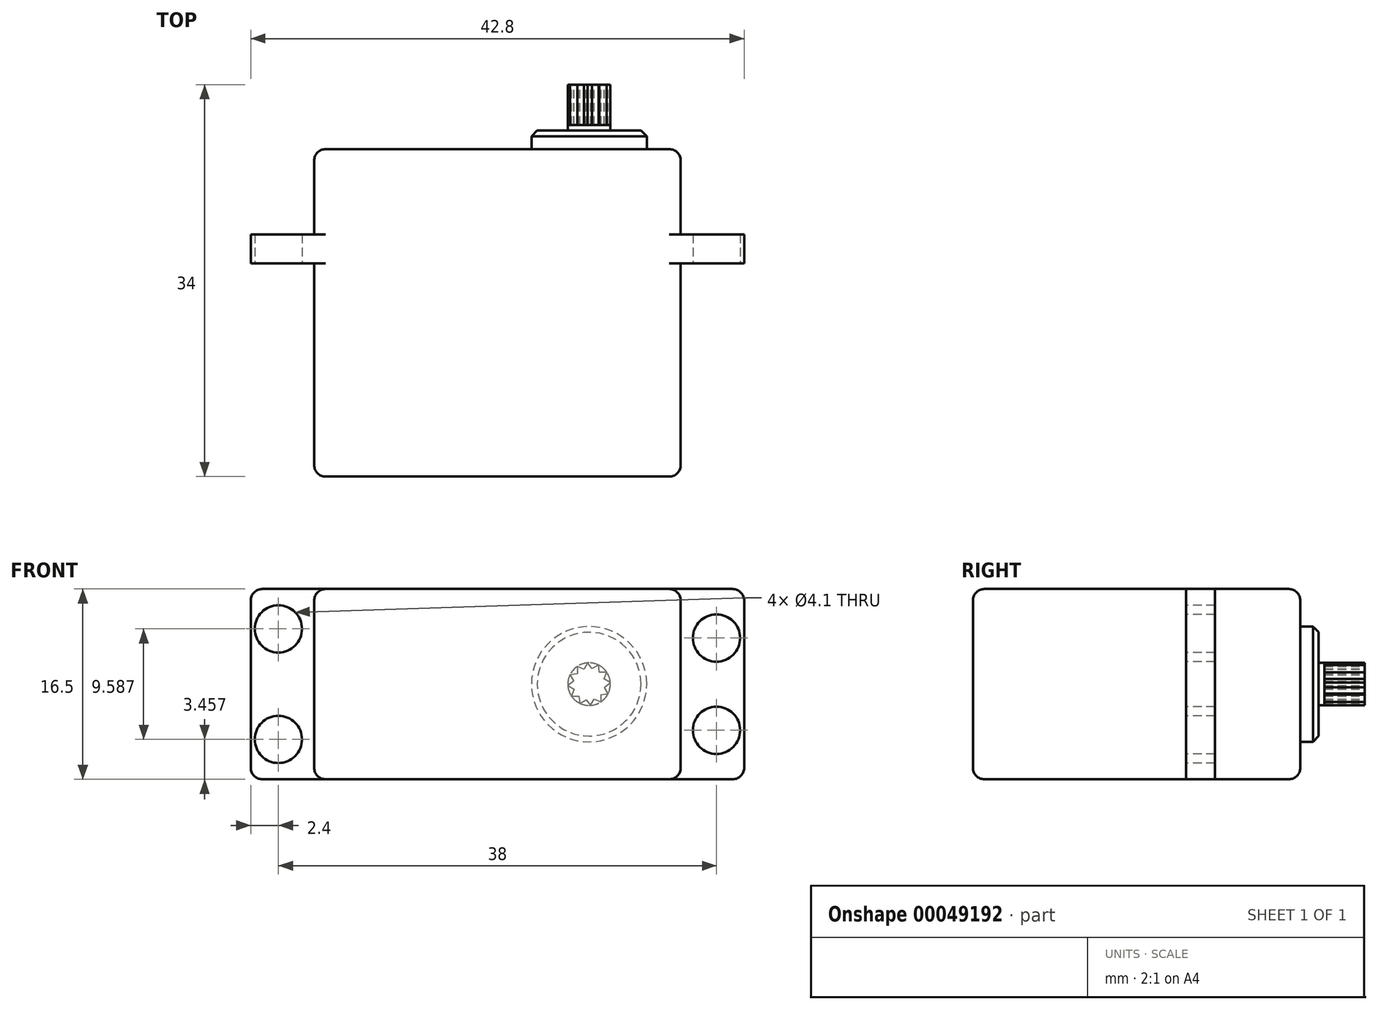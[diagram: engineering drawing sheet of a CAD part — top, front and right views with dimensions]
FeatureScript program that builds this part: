
annotation { "Feature Type Name" : "Feature", "Feature Type Description" : "" }
export const myFeature = defineFeature(function(context is Context, id is Id, definition is map)
    precondition{}
    {
        {
            var Q0;
            Q0=qCreatedBy(makeId("Top.planeOp"),FACE);
            var sketch = newSketch(context, id + "F0", { "sketchPlane" : qUnion([Q0])});
            skLineSegment(sketch, "E0.bottom", {"start": v(-15.9, 14.2) * mm, "end": v(15.9, 14.2) * mm});
            skLineSegment(sketch, "E0.top", {"start": v(-15.9, -14.2) * mm, "end": v(15.9, -14.2) * mm});
            skLineSegment(sketch, "E0.left", {"start": v(-15.9, 14.2) * mm, "end": v(-15.9, -14.2) * mm});
            skLineSegment(sketch, "E0.right", {"start": v(15.9, 14.2) * mm, "end": v(15.9, -14.2) * mm});
            skPoint(sketch, "E1", {"position": v(15.9, 0) * mm});
            skLineSegment(sketch, "E2", {"start": v(15.9, 0) * mm, "end": v(-15.9, 0) * mm, "construction": true});
            skPoint(sketch, "E3", {"position": v(0, 0) * mm});
            skLineSegment(sketch, "E4", {"start": v(-15.9, 6.8) * mm, "end": v(15.9, 6.8) * mm});
            skLineSegment(sketch, "E5", {"start": v(-15.9, 4.3) * mm, "end": v(15.9, 4.3) * mm});
            skLineSegment(sketch, "E6.left", {"start": v(-15.9, 6.8) * mm, "end": v(-15.9, 6.8) * mm});
            skLineSegment(sketch, "E7", {"start": v(-19, 4.3) * mm, "end": v(-19, 6.8) * mm, "construction": true});
            skLineSegment(sketch, "E8", {"start": v(19, 6.8) * mm, "end": v(19, 4.3) * mm, "construction": true});
            skLineSegment(sketch, "E9", {"start": v(-19, 6.8) * mm, "end": v(-21.4, 6.8) * mm});
            skLineSegment(sketch, "E10", {"start": v(-21.4, 6.8) * mm, "end": v(-21.4, 4.3) * mm});
            skLineSegment(sketch, "E11", {"start": v(-21.4, 4.3) * mm, "end": v(-19, 4.3) * mm});
            skLineSegment(sketch, "E12", {"start": v(19, 6.8) * mm, "end": v(21.4, 6.8) * mm});
            skLineSegment(sketch, "E13", {"start": v(21.4, 6.8) * mm, "end": v(21.4, 4.3) * mm});
            skLineSegment(sketch, "E14", {"start": v(21.4, 4.3) * mm, "end": v(19, 4.3) * mm});
            skLineSegment(sketch, "E15", {"start": v(-19, 6.8) * mm, "end": v(-15.9, 6.8) * mm});
            skLineSegment(sketch, "E16", {"start": v(-19, 4.3) * mm, "end": v(-15.9, 4.3) * mm});
            skLineSegment(sketch, "E17", {"start": v(15.9, 4.3) * mm, "end": v(19, 4.3) * mm});
            skLineSegment(sketch, "E18", {"start": v(15.9, 6.8) * mm, "end": v(19, 6.8) * mm});
            skSolve(sketch);
        }
        {
            var Q0;
            {var subQ2=sQuery(id+"F0.wireOp",EDGE,"E0.bottom");Q0=makeQuery(id+"F0.imprint","IMPRINT",FACE,{"disambiguationData":[TD([[makeQuery(id+"F0.imprint","IMPRINT",EDGE,{"derivedFrom":subQ2}),-1.0]])]});}
            var Q1;
            {var subQ1=sQuery(id+"F0.wireOp",EDGE,"E4");Q1=makeQuery(id+"F0.imprint","IMPRINT",FACE,{"disambiguationData":[TD([[makeQuery(id+"F0.imprint","IMPRINT",EDGE,{"derivedFrom":subQ1}),-1.0]])]});}
            var Q2;
            {var subQ2=sQuery(id+"F0.wireOp",EDGE,"E0.top");Q2=makeQuery(id+"F0.imprint","IMPRINT",FACE,{"disambiguationData":[TD([[makeQuery(id+"F0.imprint","IMPRINT",EDGE,{"derivedFrom":subQ2}),1.0]])]});}
            var Q3;
            {var subQ1=sQuery(id+"F0.wireOp",EDGE,"09e22627-e60c-491d-84b8-1f82f3b54810");Q3=makeQuery(id+"F0.imprint","IMPRINT",FACE,{"disambiguationData":[TD([[makeQuery(id+"F0.imprint","IMPRINT",EDGE,{"derivedFrom":subQ1}),1.0]])]});}
            var Q4;
            {var subQ1=sQuery(id+"F0.wireOp",EDGE,"9076f290-2de4-49c5-82f5-c9286705dbb7");Q4=makeQuery(id+"F0.imprint","IMPRINT",FACE,{"disambiguationData":[TD([[makeQuery(id+"F0.imprint","IMPRINT",EDGE,{"derivedFrom":subQ1}),-1.0]])]});}
            var Q5;
            Q5=makeQuery(id+"F0.imprint","IMPRINT",FACE,{"disambiguationData":[TD([[makeQuery(id+"F0.imprint","IMPRINT",EDGE,{"derivedFrom":sQuery(id+"F0.wireOp",EDGE,"E9")}),1.0]])]});
            var Q6;
            Q6=makeQuery(id+"F0.imprint","IMPRINT",FACE,{"disambiguationData":[TD([[makeQuery(id+"F0.imprint","IMPRINT",EDGE,{"derivedFrom":sQuery(id+"F0.wireOp",EDGE,"E12")}),-1.0]])]});
            extrude(context, id + "F1", {"entities" : qUnion([Q0, Q1, Q2, Q3, Q4, Q5, Q6]), "depth" : 16.5 * mm});
        }
        {
            var Q0;
            Q0=makeQuery(id+"F1.opExtrude","SWEPT_FACE",FACE,{"disambiguationData":[OSD([sQuery(id+"F0.wireOp",EDGE,"c4af46d5-3eda-48fc-baeb-3fe5783b968a"),sQuery(id+"F0.wireOp",EDGE,"E11")])]});
            var sketch = newSketch(context, id + "F2", { "sketchPlane" : qUnion([Q0])});
            skLineSegment(sketch, "E19.0", {"start": v(-21.4, 16.5) * mm, "end": v(-15.9, 16.5) * mm});
            skLineSegment(sketch, "E20.0", {"start": v(-19, 0) * mm, "end": v(-15.9, 0) * mm});
            skLineSegment(sketch, "E21", {"start": v(-19, 0) * mm, "end": v(-19, 16.5) * mm, "construction": true});
            skLineSegment(sketch, "E22.0", {"start": v(19, 0) * mm, "end": v(21.4, 0) * mm});
            skLineSegment(sketch, "E23.0", {"start": v(15.9, 16.5) * mm, "end": v(21.4, 16.5) * mm});
            skLineSegment(sketch, "E24", {"start": v(19, 0) * mm, "end": v(19, 16.5) * mm, "construction": true});
            skSolve(sketch);
        }
        {
            var Q0;
            {var subQ1=sQuery(id+"F0.wireOp",EDGE,"E11");Q0=makeQuery(id+"F2.imprint","IMPRINT",FACE,{"disambiguationData":[TD([[makeQuery(id+"F2.imprint","IMPRINT",EDGE,{"derivedFrom":makeQuery(id+"F1.opExtrude","SWEPT_EDGE",EDGE,{"disambiguationData":[OSD([sQuery(id+"F0.wireOp",EDGE,"E10"),subQ1])]})}),1.0]])]});}
            cPlane(context, id + "F3", {"entities" : qUnion([Q0]), "cplaneType" : CPlaneType.OFFSET, "offset" : 0 * mm, "width" : 150 * mm, "height" : 150 * mm});
        }
        {
            var Q0;
            Q0=qCreatedBy(id+"F3.planeOp",FACE);
            var sketch = newSketch(context, id + "F4", { "sketchPlane" : qUnion([Q0])});
            skLineSegment(sketch, "E25.0", {"start": v(-19, 0) * mm, "end": v(-15.9, 0) * mm});
            skPoint(sketch, "E26", {"position": v(-19, 8.25) * mm});
            skPoint(sketch, "E27", {"position": v(19, 8.25) * mm});
            skPoint(sketch, "E28.orphan", {"position": v(19, 16.5) * mm});
            skPoint(sketch, "E29.1.start.orphan", {"position": v(19, 0) * mm});
            skPoint(sketch, "E30.orphan", {"position": v(-19, 16.5) * mm});
            skPoint(sketch, "E31.0.start.orphan", {"position": v(-19, 0) * mm});
            skLineSegment(sketch, "E32", {"start": v(-19, 8.25) * mm, "end": v(-19, 13.04) * mm, "construction": true});
            skLineSegment(sketch, "E33", {"start": v(-19, 8.25) * mm, "end": v(-19, 3.46) * mm, "construction": true});
            skLineSegment(sketch, "E34", {"start": v(19, 8.25) * mm, "end": v(19, 12.25) * mm, "construction": true});
            skLineSegment(sketch, "E35", {"start": v(19, 8.25) * mm, "end": v(19, 4.25) * mm, "construction": true});
            skCircle(sketch, "E36", {"center": v(-19, 13.04) * mm, "radius": 2.05 * mm});
            skCircle(sketch, "E37", {"center": v(-19, 3.46) * mm, "radius": 2.05 * mm});
            skCircle(sketch, "E38", {"center": v(19, 12.25) * mm, "radius": 2.05 * mm});
            skCircle(sketch, "E39", {"center": v(19, 4.25) * mm, "radius": 2.05 * mm});
            skSolve(sketch);
        }
        {
            var Q0;
            Q0=qSketchRegion(id+"F4",true);
            extrude(context, id + "F5", {"entities" : qUnion([Q0]), "operationType" : NewBodyOperationType.REMOVE, "endBound" : BoundingType.THROUGH_ALL, "oppositeDirection" : true, "depth" : 25 * mm});
        }
        {
            var Q0;
            Q0=makeQuery(id+"F1.opExtrude","SWEPT_FACE",FACE,{"disambiguationData":[OSD([sQuery(id+"F0.wireOp",EDGE,"E0.bottom")])]});
            var sketch = newSketch(context, id + "F6", { "sketchPlane" : qUnion([Q0])});
            skLineSegment(sketch, "E40", {"start": v(-15.9, 8.25) * mm, "end": v(0, 8.25) * mm, "construction": true});
            skPoint(sketch, "E41.orphan", {"position": v(15.9, 8.25) * mm});
            skPoint(sketch, "E42", {"position": v(-7.95, 8.25) * mm});
            skCircle(sketch, "E43", {"center": v(-7.95, 8.25) * mm, "radius": 5 * mm});
            skLineSegment(sketch, "E44.6", {"start": v(11.12, 7.62) * mm, "end": v(11.12, 7.62) * mm});
            skLineSegment(sketch, "E44.7", {"start": v(11.12, 7.62) * mm, "end": v(11.12, 7.62) * mm});
            skLineSegment(sketch, "E44.8", {"start": v(11.12, 7.62) * mm, "end": v(11.12, 7.62) * mm});
            skLineSegment(sketch, "E44.9", {"start": v(11.12, 7.62) * mm, "end": v(11.12, 7.62) * mm});
            skLineSegment(sketch, "E44.10", {"start": v(11.12, 7.62) * mm, "end": v(11.12, 7.62) * mm});
            skLineSegment(sketch, "E44.11", {"start": v(11.12, 7.62) * mm, "end": v(11.12, 7.62) * mm});
            skLineSegment(sketch, "E44.12", {"start": v(11.12, 7.62) * mm, "end": v(11.12, 7.62) * mm});
            skLineSegment(sketch, "E44.13", {"start": v(11.12, 7.62) * mm, "end": v(11.12, 7.62) * mm});
            skLineSegment(sketch, "E44.14", {"start": v(11.12, 7.62) * mm, "end": v(11.12, 7.62) * mm});
            skLineSegment(sketch, "E44.15", {"start": v(11.12, 7.62) * mm, "end": v(11.12, 7.62) * mm});
            skLineSegment(sketch, "E44.16", {"start": v(11.12, 7.62) * mm, "end": v(11.12, 7.62) * mm});
            skLineSegment(sketch, "E44.17", {"start": v(11.12, 7.62) * mm, "end": v(11.12, 7.62) * mm});
            skLineSegment(sketch, "E44.18", {"start": v(11.12, 7.62) * mm, "end": v(11.12, 7.62) * mm});
            skLineSegment(sketch, "E44.19", {"start": v(11.12, 7.62) * mm, "end": v(11.12, 7.62) * mm});
            skCircle(sketch, "E45", {"center": v(-7.95, 8.25) * mm, "radius": 1.85 * mm});
            skSolve(sketch);
        }
        {
            var Q0;
            Q0=makeQuery(id+"F6.imprint","IMPRINT",FACE,{"disambiguationData":[TD([[makeQuery(id+"F6.imprint","IMPRINT",EDGE,{"derivedFrom":sQuery(id+"F6.wireOp",EDGE,"E43")}),1.0]])]});
            var Q1;
            Q1=makeQuery(id+"F6.imprint","IMPRINT",FACE,{"disambiguationData":[TD([[makeQuery(id+"F6.imprint","IMPRINT",EDGE,{"derivedFrom":sQuery(id+"F6.wireOp",EDGE,"E45")}),1.0]])]});
            var Q2;
            Q2=sQuery(id+"F6.wireOp",EDGE,"E43");
            extrude(context, id + "F7", {"entities" : qUnion([Q0, Q1]), "operationType" : NewBodyOperationType.ADD, "surfaceEntities" : qUnion([Q2]), "depth" : 1.6 * mm});
        }
        {
            var Q0;
            Q0=makeQuery(id+"F7.opExtrude","CAP_EDGE",EDGE,{"disambiguationData":[OSD([sQuery(id+"F6.wireOp",EDGE,"E43")])],"isStart":false});
            chamfer(context, id + "F8", {"entities" : qUnion([Q0]), "width" : 0.5 * mm, "tangentPropagation" : true});
        }
        {
            var Q0;
            Q0=makeQuery(id+"F7.opExtrude","CAP_FACE",FACE,{"disambiguationData":[OSD([sQuery(id+"F6.wireOp",EDGE,"E43")])],"isStart":false});
            var sketch = newSketch(context, id + "F9", { "sketchPlane" : qUnion([Q0])});
            skCircle(sketch, "E46.0", {"center": v(-7.95, 8.25) * mm, "radius": 1.85 * mm});
            skSolve(sketch);
        }
        {
            var Q0;
            Q0=makeQuery(id+"F9.imprint","IMPRINT",FACE,{"disambiguationData":[TD([[makeQuery(id+"F9.imprint","IMPRINT",EDGE,{"derivedFrom":sQuery(id+"F9.wireOp",EDGE,"E46.0")}),1.0]])]});
            extrude(context, id + "F10", {"entities" : qUnion([Q0]), "depth" : 4 * mm});
        }
        {
            var Q0;
            Q0=makeQuery(id+"F10.opExtrude","CAP_FACE",FACE,{"disambiguationData":[OSD([sQuery(id+"F9.wireOp",EDGE,"E46.0")])],"isStart":false});
            var sketch = newSketch(context, id + "F11", { "sketchPlane" : qUnion([Q0])});
            skCircle(sketch, "E47", {"center": v(-7.95, 8.25) * mm, "radius": 1.37 * mm});
            skLineSegment(sketch, "E48", {"start": v(-7.82, 10.1) * mm, "end": v(-7.5, 9.54) * mm});
            skLineSegment(sketch, "E49", {"start": v(-7.5, 9.54) * mm, "end": v(-6.92, 9.78) * mm});
            skLineSegment(sketch, "E50", {"start": v(-6.92, 9.78) * mm, "end": v(-6.92, 9.15) * mm});
            skLineSegment(sketch, "E51", {"start": v(-6.92, 9.15) * mm, "end": v(-6.3, 9.06) * mm});
            skLineSegment(sketch, "E52", {"start": v(-6.3, 9.06) * mm, "end": v(-6.6, 8.51) * mm});
            skLineSegment(sketch, "E53", {"start": v(-6.6, 8.51) * mm, "end": v(-6.1, 8.12) * mm});
            skLineSegment(sketch, "E54", {"start": v(-6.1, 8.12) * mm, "end": v(-6.66, 7.8) * mm});
            skLineSegment(sketch, "E55", {"start": v(-6.66, 7.8) * mm, "end": v(-6.42, 7.22) * mm});
            skLineSegment(sketch, "E56", {"start": v(-6.42, 7.22) * mm, "end": v(-7.05, 7.22) * mm});
            skLineSegment(sketch, "E57", {"start": v(-7.05, 7.22) * mm, "end": v(-7.14, 6.6) * mm});
            skLineSegment(sketch, "E58", {"start": v(-7.14, 6.6) * mm, "end": v(-7.69, 6.9) * mm});
            skLineSegment(sketch, "E59", {"start": v(-7.69, 6.9) * mm, "end": v(-8.08, 6.4) * mm});
            skLineSegment(sketch, "E60", {"start": v(-8.08, 6.4) * mm, "end": v(-8.4, 6.96) * mm});
            skLineSegment(sketch, "E61", {"start": v(-8.4, 6.96) * mm, "end": v(-8.98, 6.72) * mm});
            skLineSegment(sketch, "E62", {"start": v(-8.98, 6.72) * mm, "end": v(-8.98, 7.35) * mm});
            skLineSegment(sketch, "E63", {"start": v(-8.98, 7.35) * mm, "end": v(-9.6, 7.44) * mm});
            skLineSegment(sketch, "E64", {"start": v(-9.6, 7.44) * mm, "end": v(-9.3, 7.99) * mm});
            skLineSegment(sketch, "E65", {"start": v(-9.3, 7.99) * mm, "end": v(-9.8, 8.38) * mm});
            skLineSegment(sketch, "E66", {"start": v(-9.48, 9.28) * mm, "end": v(-8.85, 9.28) * mm});
            skLineSegment(sketch, "E67", {"start": v(-8.85, 9.28) * mm, "end": v(-8.76, 9.9) * mm});
            skLineSegment(sketch, "E68", {"start": v(-8.76, 9.9) * mm, "end": v(-8.21, 9.6) * mm});
            skLineSegment(sketch, "E69", {"start": v(-8.21, 9.6) * mm, "end": v(-7.82, 10.1) * mm});
            skLineSegment(sketch, "E70", {"start": v(-9.8, 8.38) * mm, "end": v(-9.24, 8.7) * mm});
            skLineSegment(sketch, "E71", {"start": v(-9.24, 8.7) * mm, "end": v(-9.48, 9.28) * mm});
            skSolve(sketch);
        }
        {
            var Q0;
            {var subQ2=sQuery(id+"F11.wireOp",EDGE,"E66");Q0=makeQuery(id+"F11.imprint","IMPRINT",FACE,{"disambiguationData":[TD([[makeQuery(id+"F11.imprint","IMPRINT",EDGE,{"derivedFrom":subQ2}),1.0]])]});}
            var Q1;
            {var subQ2=sQuery(id+"F11.wireOp",EDGE,"E70");Q1=makeQuery(id+"F11.imprint","IMPRINT",FACE,{"disambiguationData":[TD([[makeQuery(id+"F11.imprint","IMPRINT",EDGE,{"derivedFrom":subQ2}),1.0]])]});}
            var Q2;
            {var subQ2=sQuery(id+"F11.wireOp",EDGE,"E64");Q2=makeQuery(id+"F11.imprint","IMPRINT",FACE,{"disambiguationData":[TD([[makeQuery(id+"F11.imprint","IMPRINT",EDGE,{"derivedFrom":subQ2}),1.0]])]});}
            var Q3;
            {var subQ2=sQuery(id+"F11.wireOp",EDGE,"E62");Q3=makeQuery(id+"F11.imprint","IMPRINT",FACE,{"disambiguationData":[TD([[makeQuery(id+"F11.imprint","IMPRINT",EDGE,{"derivedFrom":subQ2}),1.0]])]});}
            var Q4;
            {var subQ2=sQuery(id+"F11.wireOp",EDGE,"E60");Q4=makeQuery(id+"F11.imprint","IMPRINT",FACE,{"disambiguationData":[TD([[makeQuery(id+"F11.imprint","IMPRINT",EDGE,{"derivedFrom":subQ2}),1.0]])]});}
            var Q5;
            {var subQ2=sQuery(id+"F11.wireOp",EDGE,"E58");Q5=makeQuery(id+"F11.imprint","IMPRINT",FACE,{"disambiguationData":[TD([[makeQuery(id+"F11.imprint","IMPRINT",EDGE,{"derivedFrom":subQ2}),1.0]])]});}
            var Q6;
            {var subQ2=sQuery(id+"F11.wireOp",EDGE,"E56");Q6=makeQuery(id+"F11.imprint","IMPRINT",FACE,{"disambiguationData":[TD([[makeQuery(id+"F11.imprint","IMPRINT",EDGE,{"derivedFrom":subQ2}),1.0]])]});}
            var Q7;
            {var subQ2=sQuery(id+"F11.wireOp",EDGE,"E54");Q7=makeQuery(id+"F11.imprint","IMPRINT",FACE,{"disambiguationData":[TD([[makeQuery(id+"F11.imprint","IMPRINT",EDGE,{"derivedFrom":subQ2}),1.0]])]});}
            var Q8;
            {var subQ2=sQuery(id+"F11.wireOp",EDGE,"E52");Q8=makeQuery(id+"F11.imprint","IMPRINT",FACE,{"disambiguationData":[TD([[makeQuery(id+"F11.imprint","IMPRINT",EDGE,{"derivedFrom":subQ2}),1.0]])]});}
            var Q9;
            {var subQ2=sQuery(id+"F11.wireOp",EDGE,"E50");Q9=makeQuery(id+"F11.imprint","IMPRINT",FACE,{"disambiguationData":[TD([[makeQuery(id+"F11.imprint","IMPRINT",EDGE,{"derivedFrom":subQ2}),1.0]])]});}
            var Q10;
            {var subQ2=sQuery(id+"F11.wireOp",EDGE,"E48");Q10=makeQuery(id+"F11.imprint","IMPRINT",FACE,{"disambiguationData":[TD([[makeQuery(id+"F11.imprint","IMPRINT",EDGE,{"derivedFrom":subQ2}),1.0]])]});}
            var Q11;
            {var subQ1=sQuery(id+"F11.wireOp",EDGE,"E68");Q11=makeQuery(id+"F11.imprint","IMPRINT",FACE,{"disambiguationData":[TD([[makeQuery(id+"F11.imprint","IMPRINT",EDGE,{"derivedFrom":subQ1}),1.0]])]});}
            extrude(context, id + "F12", {"entities" : qUnion([Q0, Q1, Q2, Q3, Q4, Q5, Q6, Q7, Q8, Q9, Q10, Q11]), "operationType" : NewBodyOperationType.REMOVE, "oppositeDirection" : true, "depth" : 3.5 * mm});
        }
        {
            var Q0;
            Q0=makeQuery(id+"F1.opExtrude","SWEPT_FACE",FACE,{"disambiguationData":[OSD([sQuery(id+"F0.wireOp",EDGE,"E0.top")])]});
            var Q1;
            Q1=makeQuery(id+"F1.opExtrude","CAP_EDGE",EDGE,{"disambiguationData":[OSD([sQuery(id+"F0.wireOp",EDGE,"E0.bottom")])],"isStart":false});
            var Q2;
            {var subQ0=sQuery(id+"F0.wireOp",EDGE,"E0.right");Q2=makeQuery(id+"F1.opExtrude","CAP_EDGE",EDGE,{"disambiguationData":[OSD([subQ0]),TDD([makeQuery(id+"F0.imprint","IMPRINT",EDGE,{"disambiguationData":[TD([[makeQuery(id+"F0.imprint","INTERSECT",VERTEX,{"derivedFrom":[sQuery(id+"F0.wireOp",EDGE,"E0.top"),subQ0]}),1.0]])],"derivedFrom":subQ0})])],"isStart":false});}
            var Q3;
            {var subQ0=sQuery(id+"F0.wireOp",EDGE,"E0.right");Q3=makeQuery(id+"F1.opExtrude","CAP_EDGE",EDGE,{"disambiguationData":[OSD([subQ0]),TDD([makeQuery(id+"F0.imprint","IMPRINT",EDGE,{"disambiguationData":[TD([[makeQuery(id+"F0.imprint","INTERSECT",VERTEX,{"derivedFrom":[sQuery(id+"F0.wireOp",EDGE,"E0.top"),subQ0]}),1.0]])],"derivedFrom":subQ0})])],"isStart":true});}
            var Q4;
            {var subQ0=sQuery(id+"F0.wireOp",EDGE,"E0.left");Q4=makeQuery(id+"F1.opExtrude","CAP_EDGE",EDGE,{"disambiguationData":[OSD([subQ0]),TDD([makeQuery(id+"F0.imprint","IMPRINT",EDGE,{"disambiguationData":[TD([[makeQuery(id+"F0.imprint","INTERSECT",VERTEX,{"derivedFrom":[sQuery(id+"F0.wireOp",EDGE,"E0.top"),subQ0]}),1.0]])],"derivedFrom":subQ0})])],"isStart":true});}
            var Q5;
            {var subQ0=sQuery(id+"F0.wireOp",EDGE,"E0.left");Q5=makeQuery(id+"F1.opExtrude","CAP_EDGE",EDGE,{"disambiguationData":[OSD([subQ0]),TDD([makeQuery(id+"F0.imprint","IMPRINT",EDGE,{"disambiguationData":[TD([[makeQuery(id+"F0.imprint","INTERSECT",VERTEX,{"derivedFrom":[sQuery(id+"F0.wireOp",EDGE,"E0.top"),subQ0]}),1.0]])],"derivedFrom":subQ0})])],"isStart":false});}
            var Q6;
            Q6=makeQuery(id+"F1.opExtrude","SWEPT_EDGE",EDGE,{"disambiguationData":[OSD([sQuery(id+"F0.wireOp",EDGE,"E0.bottom"),sQuery(id+"F0.wireOp",EDGE,"E0.left")])]});
            var Q7;
            Q7=makeQuery(id+"F1.opExtrude","CAP_EDGE",EDGE,{"disambiguationData":[OSD([sQuery(id+"F0.wireOp",EDGE,"E0.bottom")])],"isStart":true});
            var Q8;
            {var subQ0=sQuery(id+"F0.wireOp",EDGE,"E0.right");Q8=makeQuery(id+"F1.opExtrude","CAP_EDGE",EDGE,{"disambiguationData":[OSD([subQ0]),TDD([makeQuery(id+"F0.imprint","IMPRINT",EDGE,{"disambiguationData":[TD([[makeQuery(id+"F0.imprint","INTERSECT",VERTEX,{"derivedFrom":[sQuery(id+"F0.wireOp",EDGE,"E0.bottom"),subQ0]}),-1.0]])],"derivedFrom":subQ0})])],"isStart":true});}
            var Q9;
            {var subQ0=sQuery(id+"F0.wireOp",EDGE,"E0.right");Q9=makeQuery(id+"F1.opExtrude","CAP_EDGE",EDGE,{"disambiguationData":[OSD([subQ0]),TDD([makeQuery(id+"F0.imprint","IMPRINT",EDGE,{"disambiguationData":[TD([[makeQuery(id+"F0.imprint","INTERSECT",VERTEX,{"derivedFrom":[sQuery(id+"F0.wireOp",EDGE,"E0.bottom"),subQ0]}),-1.0]])],"derivedFrom":subQ0})])],"isStart":false});}
            var Q10;
            Q10=makeQuery(id+"F1.opExtrude","CAP_EDGE",EDGE,{"disambiguationData":[OSD([sQuery(id+"F0.wireOp",EDGE,"E13")])],"isStart":false});
            var Q11;
            Q11=makeQuery(id+"F1.opExtrude","CAP_EDGE",EDGE,{"disambiguationData":[OSD([sQuery(id+"F0.wireOp",EDGE,"E13")])],"isStart":true});
            var Q12;
            Q12=makeQuery(id+"F1.opExtrude","CAP_EDGE",EDGE,{"disambiguationData":[OSD([sQuery(id+"F0.wireOp",EDGE,"E10")])],"isStart":true});
            var Q13;
            Q13=makeQuery(id+"F1.opExtrude","CAP_EDGE",EDGE,{"disambiguationData":[OSD([sQuery(id+"F0.wireOp",EDGE,"E10")])],"isStart":false});
            var Q14;
            {var subQ0=sQuery(id+"F0.wireOp",EDGE,"E0.left");Q14=makeQuery(id+"F1.opExtrude","CAP_EDGE",EDGE,{"disambiguationData":[OSD([subQ0]),TDD([makeQuery(id+"F0.imprint","IMPRINT",EDGE,{"disambiguationData":[TD([[makeQuery(id+"F0.imprint","INTERSECT",VERTEX,{"derivedFrom":[sQuery(id+"F0.wireOp",EDGE,"E0.bottom"),subQ0]}),-1.0]])],"derivedFrom":subQ0})])],"isStart":false});}
            var Q15;
            {var subQ0=sQuery(id+"F0.wireOp",EDGE,"E0.left");Q15=makeQuery(id+"F1.opExtrude","CAP_EDGE",EDGE,{"disambiguationData":[OSD([subQ0]),TDD([makeQuery(id+"F0.imprint","IMPRINT",EDGE,{"disambiguationData":[TD([[makeQuery(id+"F0.imprint","INTERSECT",VERTEX,{"derivedFrom":[sQuery(id+"F0.wireOp",EDGE,"E0.bottom"),subQ0]}),-1.0]])],"derivedFrom":subQ0})])],"isStart":true});}
            var Q16;
            Q16=makeQuery(id+"F1.opExtrude","SWEPT_EDGE",EDGE,{"disambiguationData":[OSD([sQuery(id+"F0.wireOp",EDGE,"E0.bottom"),sQuery(id+"F0.wireOp",EDGE,"E0.right")])]});
            fillet(context, id + "F13", {"entities" : qUnion([Q0, Q1, Q2, Q3, Q4, Q5, Q6, Q7, Q8, Q9, Q10, Q11, Q12, Q13, Q14, Q15, Q16]), "radius" : 1 * mm, "allowEdgeOverflow" : false});
        }
    });
